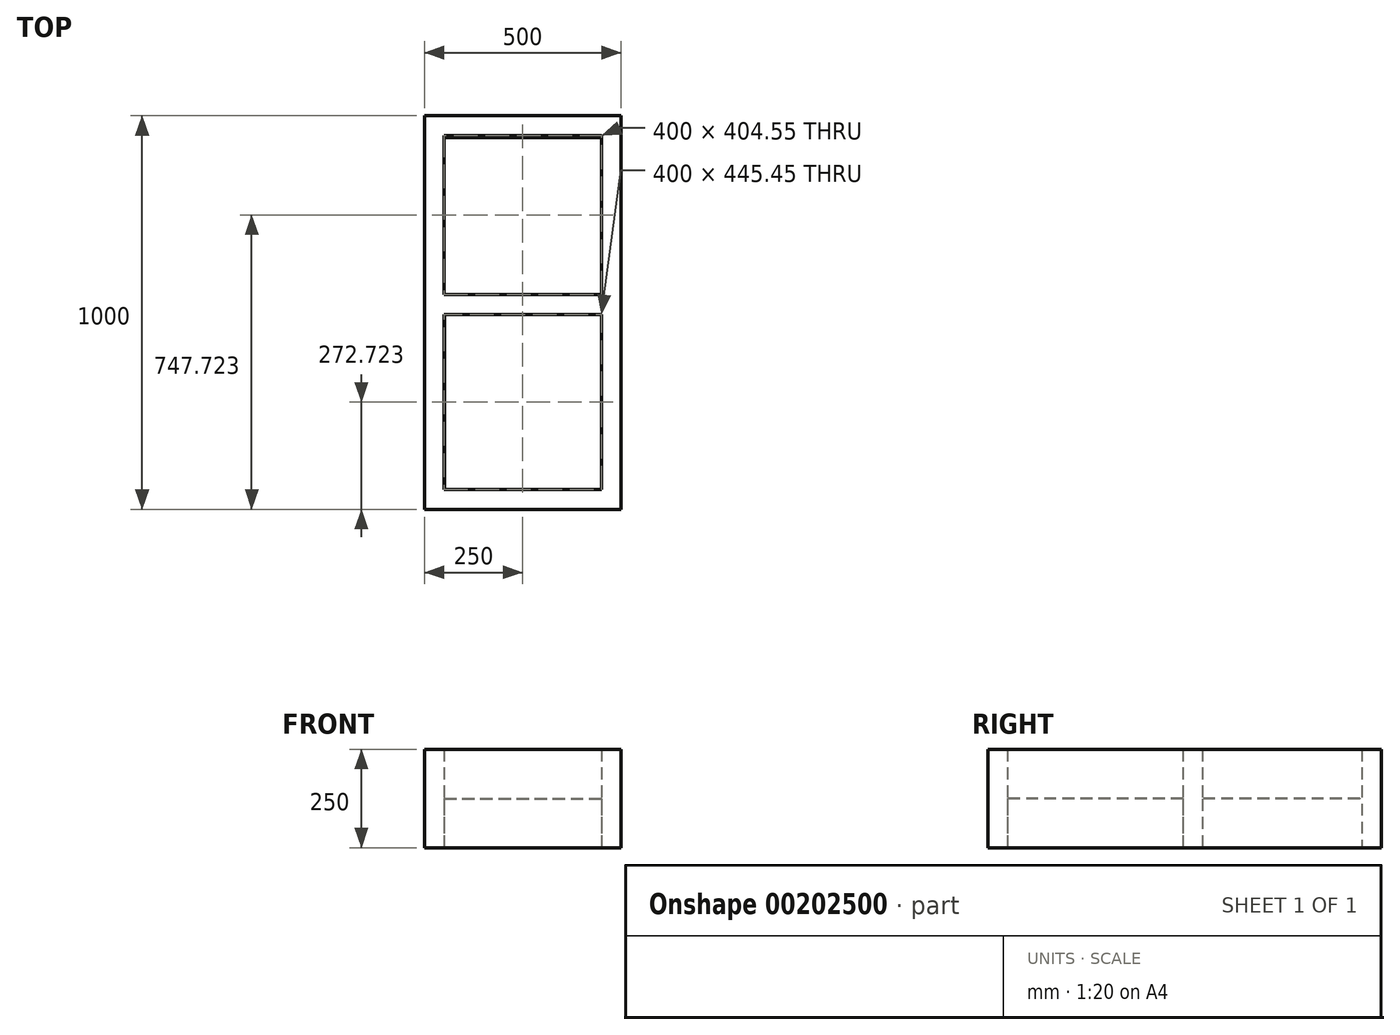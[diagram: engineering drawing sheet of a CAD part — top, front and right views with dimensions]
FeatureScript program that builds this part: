
annotation { "Feature Type Name" : "Feature", "Feature Type Description" : "" }
export const myFeature = defineFeature(function(context is Context, id is Id, definition is map)
    precondition{}
    {
        {
            var Q0;
            Q0=qCreatedBy(makeId("Top.planeOp"),FACE);
            var sketch = newSketch(context, id + "F0", { "sketchPlane" : qUnion([Q0])});
            skLineSegment(sketch, "E0.bottom", {"start": v(250, 500) * mm, "end": v(-250, 500) * mm});
            skLineSegment(sketch, "E0.top", {"start": v(250, -500) * mm, "end": v(-250, -500) * mm});
            skLineSegment(sketch, "E0.left", {"start": v(250, 500) * mm, "end": v(250, -500) * mm});
            skLineSegment(sketch, "E0.right", {"start": v(-250, 500) * mm, "end": v(-250, -500) * mm});
            skPoint(sketch, "E0.middle", {"position": v(0, 0) * mm});
            skLineSegment(sketch, "E1.bottom", {"start": v(-200, 450) * mm, "end": v(200, 450) * mm});
            skLineSegment(sketch, "E1.top", {"start": v(-200, 45.45) * mm, "end": v(200, 45.45) * mm});
            skLineSegment(sketch, "E1.left", {"start": v(-200, 450) * mm, "end": v(-200, 45.45) * mm});
            skLineSegment(sketch, "E1.right", {"start": v(200, 450) * mm, "end": v(200, 45.45) * mm});
            skLineSegment(sketch, "E2.bottom", {"start": v(-200, -4.55) * mm, "end": v(200, -4.55) * mm});
            skLineSegment(sketch, "E2.top", {"start": v(-200, -450) * mm, "end": v(200, -450) * mm});
            skLineSegment(sketch, "E2.left", {"start": v(-200, -4.55) * mm, "end": v(-200, -450) * mm});
            skLineSegment(sketch, "E2.right", {"start": v(200, -4.55) * mm, "end": v(200, -450) * mm});
            skSolve(sketch);
        }
        {
            var Q0;
            Q0=makeQuery(id+"F0.imprint","IMPRINT",FACE,{"disambiguationData":[TD([[makeQuery(id+"F0.imprint","IMPRINT",EDGE,{"derivedFrom":sQuery(id+"F0.wireOp",EDGE,"E0.bottom")}),1.0]])]});
            extrude(context, id + "F1", {"entities" : qUnion([Q0]), "endBound" : BoundingType.SYMMETRIC, "depth" : 250 * mm});
        }
        {
            var Q0;
            Q0=qCreatedBy(makeId("Top.planeOp"),FACE);
            var sketch = newSketch(context, id + "F2", { "sketchPlane" : qUnion([Q0])});
            skLineSegment(sketch, "E3.bottom", {"start": v(-200, 445) * mm, "end": v(201.62, 445) * mm});
            skLineSegment(sketch, "E3.top", {"start": v(-200, 45) * mm, "end": v(201.62, 45) * mm});
            skLineSegment(sketch, "E3.left", {"start": v(-200, 445) * mm, "end": v(-200, 45) * mm});
            skLineSegment(sketch, "E3.right", {"start": v(201.62, 445) * mm, "end": v(201.62, 45) * mm});
            skLineSegment(sketch, "E4.bottom", {"start": v(-198.38, 0) * mm, "end": v(201.62, 0) * mm});
            skLineSegment(sketch, "E4.top", {"start": v(-198.38, -450) * mm, "end": v(201.62, -450) * mm});
            skLineSegment(sketch, "E4.left", {"start": v(-198.38, 0) * mm, "end": v(-198.38, -450) * mm});
            skLineSegment(sketch, "E4.right", {"start": v(201.62, 0) * mm, "end": v(201.62, -450) * mm});
            skSolve(sketch);
        }
        {
            var Q0;
            Q0=qSketchRegion(id+"F2",true);
            extrude(context, id + "F3", {"entities" : qUnion([Q0]), "operationType" : NewBodyOperationType.ADD, "endBound" : BoundingType.SYMMETRIC, "depth" : 2 * mm});
        }
    });
